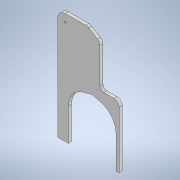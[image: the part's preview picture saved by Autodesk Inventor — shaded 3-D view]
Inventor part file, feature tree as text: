
AUTODESK INVENTOR PART (.ipt)
format: ipt  version: 2020 (Build 240168000, 168)  size: 137,728 bytes
history: native  units: mm
features: other x10, extrude x1, sketch x1
ambient origin geometry x8: Origin, YZ Plane, XZ Plane, XY Plane, X Axis, Y Axis, Z Axis, Center Point
bodies: Body1 (feature_tree)
feature tree (12):
  other  "Sólido1"
  extrude  "Extrusão1"  Depth=20.0mm
  sketch  "Esboço1"  dims[d4=3.0mm d5=0.0mm d7=20.0mm d9=5.0mm d11=5.0mm]
  other  "Referência1"
  other  "Referência2"
  other  "Referência7"
  other  "<userpath>\Desktop\rabo\3d\ela.iam"
  other  "ela.iam"
  other  "eixo:1"
  other  "basesinha:1"
  other  "56145_Wheel_MIR:1"
  other  "Component2_32_MIR:1"
